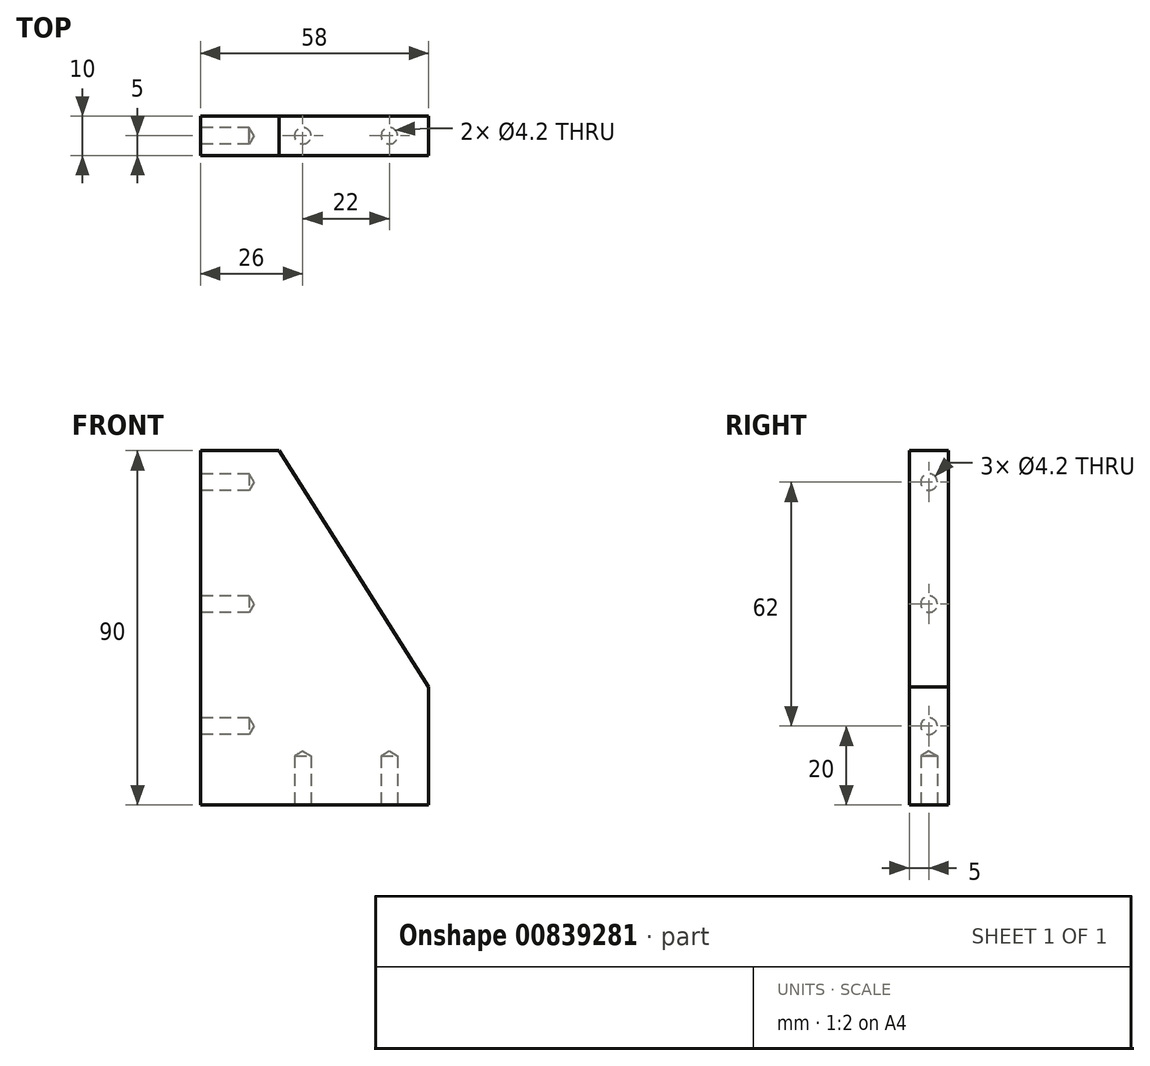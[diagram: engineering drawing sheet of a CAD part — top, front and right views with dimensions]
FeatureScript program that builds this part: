
annotation { "Feature Type Name" : "Feature", "Feature Type Description" : "" }
export const myFeature = defineFeature(function(context is Context, id is Id, definition is map)
    precondition{}
    {
        {
            var Q0;
            Q0=qCreatedBy(makeId("Front.planeOp"),FACE);
            var sketch = newSketch(context, id + "F0", { "sketchPlane" : qUnion([Q0])});
            skLineSegment(sketch, "E0", {"start": v(0, 0) * mm, "end": v(58, 0) * mm});
            skLineSegment(sketch, "E1", {"start": v(0, 0) * mm, "end": v(0, 90) * mm});
            skLineSegment(sketch, "E2", {"start": v(58, 0) * mm, "end": v(58, 30) * mm});
            skLineSegment(sketch, "E3", {"start": v(0, 90) * mm, "end": v(20, 90) * mm});
            skLineSegment(sketch, "E4", {"start": v(20, 90) * mm, "end": v(58, 30) * mm});
            skSolve(sketch);
        }
        {
            var Q0;
            Q0=makeQuery(id+"F0.imprint","IMPRINT",FACE,{"disambiguationData":[TD([[makeQuery(id+"F0.imprint","IMPRINT",EDGE,{"derivedFrom":sQuery(id+"F0.wireOp",EDGE,"E0")}),1.0]])]});
            extrude(context, id + "F1", {"entities" : qUnion([Q0]), "endBound" : BoundingType.SYMMETRIC, "depth" : 10 * mm, "offsetDistance" : 25 * mm});
        }
        {
            var Q0;
            Q0=makeQuery(id+"F1.opExtrude","SWEPT_FACE",FACE,{"disambiguationData":[OSD([sQuery(id+"F0.wireOp",EDGE,"E0")])]});
            var sketch = newSketch(context, id + "F2", { "sketchPlane" : qUnion([Q0])});
            skPoint(sketch, "E5", {"position": v(48, 0) * mm});
            skPoint(sketch, "E5.positionSnap0", {"position": v(58, 0) * mm});
            skPoint(sketch, "E6", {"position": v(26, 0) * mm});
            skSolve(sketch);
        }
        {
            var Q0;
            Q0=sQuery(id+"F2.wireOp",VERTEX,"61244e3f-df29-4a6c-b4fe-e90460b9aaec");
            var Q1;
            Q1=sQuery(id+"F2.wireOp",VERTEX,"e48956c4-2f93-4645-9aed-4df6b440663b");
            var Q2;
            Q2=sQuery(id+"F2.wireOp",VERTEX,"E6");
            var Q3;
            Q3=sQuery(id+"F2.wireOp",VERTEX,"E5");
            var Q4;
            Q4=makeQuery(id+"F1.opExtrude","SWEPT_BODY",BODY,{"disambiguationData":[OSD([sQuery(id+"F0.wireOp",EDGE,"E0"),sQuery(id+"F0.wireOp",EDGE,"E1"),sQuery(id+"F0.wireOp",EDGE,"NgpiGnQK-4uB7-JLf6-VrBV-Ro4ZOfoehQ1u")])]});
            hole(context, id + "F3", {"style" : HoleStyle.SIMPLE, "endStyle" : HoleEndStyle.BLIND, "standardTappedOrClearance" : lookupTablePath({ "standard" : "ISO", "engagement" : "75%", "pitch" : "0.8 mm", "size" : "M5", "type" : "Tapped" }), "standardBlindInLast" : lookupTablePath({ "standard" : "ISO", "fit" : "Normal", "engagement" : "75%", "pitch" : "0.8 mm", "size" : "M5", "type" : "Clearance & tapped" }), "holeDiameter" : 4.2 * mm, "majorDiameter" : 5 * mm, "showTappedDepth" : true, "holeDepth" : 12.4 * mm, "isTappedThrough" : true, "tappedDepth" : 10 * mm, "tapClearance" : 3, "locations" : qUnion([Q0, Q1, Q2, Q3]), "scope" : qUnion([Q4])});
        }
        {
            var Q0;
            Q0=makeQuery(id+"F1.opExtrude","SWEPT_FACE",FACE,{"disambiguationData":[OSD([sQuery(id+"F0.wireOp",EDGE,"E1")])]});
            var sketch = newSketch(context, id + "F4", { "sketchPlane" : qUnion([Q0])});
            skPoint(sketch, "E7", {"position": v(0, 20) * mm});
            skPoint(sketch, "E8", {"position": v(0, 82) * mm});
            skPoint(sketch, "E9", {"position": v(0, 51) * mm});
            skSolve(sketch);
        }
        {
            var Q0;
            Q0=sQuery(id+"F4.wireOp",VERTEX,"E7");
            var Q1;
            Q1=sQuery(id+"F4.wireOp",VERTEX,"E8");
            var Q2;
            Q2=sQuery(id+"F4.wireOp",VERTEX,"E9");
            var Q3;
            Q3=makeQuery(id+"F1.opExtrude","SWEPT_BODY",BODY,{"disambiguationData":[OSD([sQuery(id+"F0.wireOp",EDGE,"E0"),sQuery(id+"F0.wireOp",EDGE,"E1"),sQuery(id+"F0.wireOp",EDGE,"NgpiGnQK-4uB7-JLf6-VrBV-Ro4ZOfoehQ1u")])]});
            hole(context, id + "F5", {"style" : HoleStyle.SIMPLE, "endStyle" : HoleEndStyle.BLIND, "standardTappedOrClearance" : lookupTablePath({ "standard" : "ISO", "engagement" : "75%", "pitch" : "0.8 mm", "size" : "M5", "type" : "Tapped" }), "standardBlindInLast" : lookupTablePath({ "standard" : "ISO", "fit" : "Normal", "engagement" : "75%", "pitch" : "0.8 mm", "size" : "M5", "type" : "Clearance & tapped" }), "holeDiameter" : 4.2 * mm, "majorDiameter" : 5 * mm, "showTappedDepth" : true, "holeDepth" : 12.4 * mm, "isTappedThrough" : true, "tappedDepth" : 10 * mm, "tapClearance" : 3, "locations" : qUnion([Q0, Q1, Q2]), "scope" : qUnion([Q3])});
        }
    });
